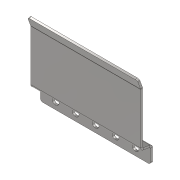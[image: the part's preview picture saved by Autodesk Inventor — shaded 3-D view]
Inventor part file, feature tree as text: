
AUTODESK INVENTOR PART (.ipt)
format: ipt  version: 2020 (Build 240168000, 168)  size: 217,600 bytes
history: native  units: mm
features: sheet_metal_op x8, sketch x5, other x5, projected_geometry x2, fillet x1
ambient origin geometry x8: Origin, YZ Plane, XZ Plane, XY Plane, X Axis, Y Axis, Z Axis, Center Point
bodies: Solid1 (feature_tree)
feature tree (21):
  sheet_metal_op  "Face1"
  sheet_metal_op  "Flange1"
  sheet_metal_op  "Flange2"
  fillet  "Fillet1"  Radius=110.0mm
  sheet_metal_op  "Fold1"
  sketch  "Sketch1"  dims[d1=15.0mm]
  other  "Plate1"
  sketch  "Sketch2"  dims[d2=2.0mm]
  other  "Plate2"
  sheet_metal_op  "Bend1"
  sheet_metal_op  "Corner1"
  sketch  "Sketch3"  dims[d3=2.0mm]
  other  "Plate3"
  sheet_metal_op  "Bend2"
  sheet_metal_op  "Corner2"
  sketch  "Sketch4"  dims[d4=1.0mm]
  projected_geometry  "Projected Loop1"
  sketch  "Sketch5"  dims[d5=4.0mm d6=2.0mm d7=10.0mm d8=13.962634mm d9=1.0mm d10=8.0mm d11=2.0mm d12=2.0mm d13=2.0mm d14=1.0mm d15=4.0mm d16=2.0mm d17=63.264mm d18=13.962634mm d19=1.0mm d20=8.0mm d21=2.0mm d22=2.0mm d23=7.0mm d24=30.0mm d26=20.0mm d27=10.0mm d29=10.0mm d31=30.0mm d33=20.0mm d34=10.0mm d36=10.0mm d38=2.0mm d39=0.0mm d40=2.0mm d41=10.0mm d42=2.0mm d43=1.0mm d44=4.0mm d45=2.0mm d46=3.490659mm d47=1.0mm]
  projected_geometry  "Projected Loop2"
  other  "Cut1"
  other  "Definition1"
